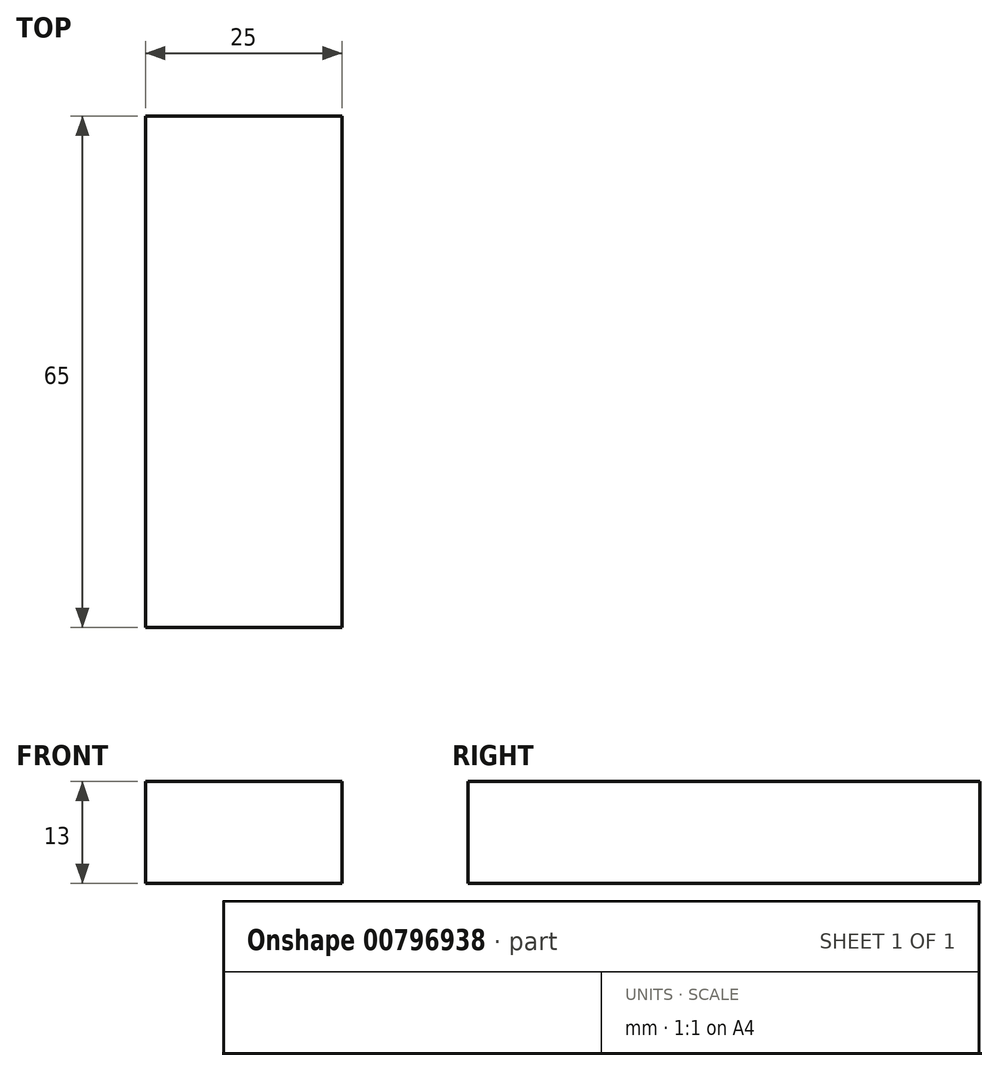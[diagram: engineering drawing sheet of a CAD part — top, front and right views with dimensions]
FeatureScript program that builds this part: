
annotation { "Feature Type Name" : "Feature", "Feature Type Description" : "" }
export const myFeature = defineFeature(function(context is Context, id is Id, definition is map)
    precondition{}
    {
        {
            var Q0;
            Q0=qCreatedBy(makeId("Top.planeOp"),FACE);
            var sketch = newSketch(context, id + "F0", { "sketchPlane" : qUnion([Q0])});
            skLineSegment(sketch, "E0.bottom", {"start": v(12.5, 32.5) * mm, "end": v(-12.5, 32.5) * mm});
            skLineSegment(sketch, "E0.top", {"start": v(12.5, -32.5) * mm, "end": v(-12.5, -32.5) * mm});
            skLineSegment(sketch, "E0.left", {"start": v(12.5, 32.5) * mm, "end": v(12.5, -32.5) * mm});
            skLineSegment(sketch, "E0.right", {"start": v(-12.5, 32.5) * mm, "end": v(-12.5, -32.5) * mm});
            skPoint(sketch, "E0.middle", {"position": v(0, 0) * mm});
            skSolve(sketch);
        }
        {
            var Q0;
            Q0 = qSketchRegion(id + "F0", true);
            extrude(context, id + "F1", {"entities" : qUnion([Q0]), "depth" : 13 * mm, "offsetDistance" : 25 * mm});
        }
    });
